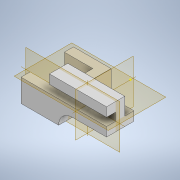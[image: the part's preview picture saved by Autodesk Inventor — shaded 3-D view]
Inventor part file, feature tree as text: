
AUTODESK INVENTOR PART (.ipt)
format: ipt  version: 2022.4 (Build 264492010, 492A)  size: 166,400 bytes
history: native  units: mm
features: extrude x4, sketch x4
ambient origin geometry x8: Origin, YZ Plane, XZ Plane, XY Plane, X Axis, Y Axis, Z Axis, Center Point
bodies: Solid1 (feature_tree)
feature tree (8):
  extrude  "Extrusion1"  Depth=3.0mm
  extrude  "Extrusion2"  Depth=1.6mm
  sketch  "Sketch4"  dims[d3=3.2mm d4=1.6mm]
  sketch  "Sketch5"  dims[d6=4.0mm d7=1.6mm]
  extrude  "Extrusion3"  Depth=1.6mm
  extrude  "Extrusion4"  Depth=10.0mm TaperAngle=0.0deg
  sketch  "Sketch3"  dims[d1=6.0mm d2=3.0mm]
  sketch  "Sketch6"  dims[d8=1.4mm d10=10.0mm d11=0.0mm d12=1.6mm d14=1.6mm d15=1.6mm d17=2.4mm d18=0.0mm d19=0.0mm d20=1.6mm d21=1.6mm d22=5.0mm d23=0.0mm d24=1.6mm d25=1.6mm d26=1.6mm d27=0.0mm d28=0.0mm]
